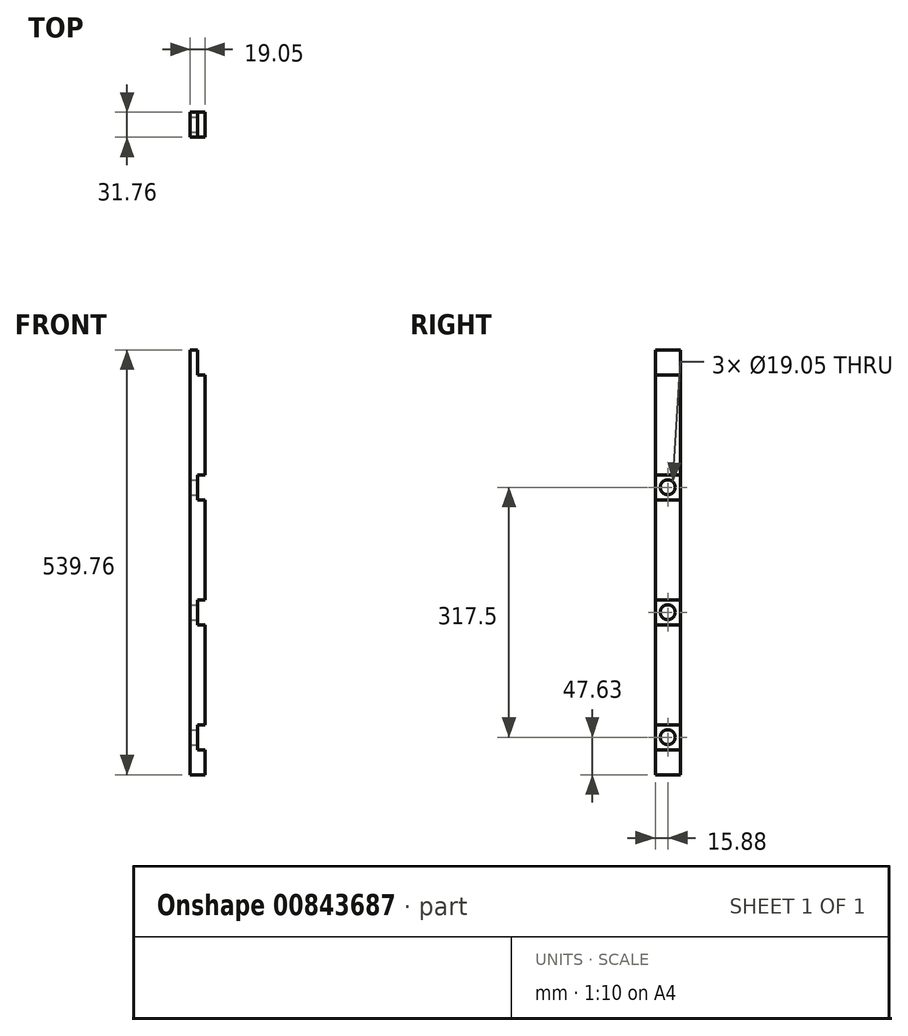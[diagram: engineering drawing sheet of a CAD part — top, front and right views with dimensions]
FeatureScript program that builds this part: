
annotation { "Feature Type Name" : "Feature", "Feature Type Description" : "" }
export const myFeature = defineFeature(function(context is Context, id is Id, definition is map)
    precondition{}
    {
        {
            var Q0;
            Q0=qCreatedBy(makeId("Right.planeOp"),FACE);
            var sketch = newSketch(context, id + "F0", { "sketchPlane" : qUnion([Q0])});
            skLineSegment(sketch, "E0.bottom", {"start": v(15.88, 269.88) * mm, "end": v(-15.87, 269.88) * mm});
            skLineSegment(sketch, "E0.top", {"start": v(15.88, -269.88) * mm, "end": v(-15.87, -269.88) * mm});
            skLineSegment(sketch, "E0.left", {"start": v(15.88, 269.88) * mm, "end": v(15.88, -269.88) * mm});
            skLineSegment(sketch, "E0.right", {"start": v(-15.87, 269.88) * mm, "end": v(-15.87, -269.88) * mm});
            skPoint(sketch, "E0.middle", {"position": v(0, 0) * mm});
            skSolve(sketch);
        }
        {
            var Q0;
            Q0 = qSketchRegion(id + "F0", true);
            extrude(context, id + "F1", {"entities" : qUnion([Q0]), "depth" : 19.05 * mm, "offsetDistance" : 25.4 * mm});
        }
        {
            var Q0;
            Q0=makeQuery(id+"F1.opExtrude","CAP_FACE",FACE,{"disambiguationData":[OSD([sQuery(id+"F0.wireOp",EDGE,"E0.bottom"),sQuery(id+"F0.wireOp",EDGE,"E0.top"),sQuery(id+"F0.wireOp",EDGE,"E0.left"),sQuery(id+"F0.wireOp",EDGE,"E0.right")])],"isStart":false});
            var sketch = newSketch(context, id + "F2", { "sketchPlane" : qUnion([Q0])});
            skLineSegment(sketch, "E1.bottom", {"start": v(-15.87, 269.88) * mm, "end": v(15.88, 269.88) * mm});
            skLineSegment(sketch, "E1.top", {"start": v(-15.87, 238.13) * mm, "end": v(15.88, 238.13) * mm});
            skLineSegment(sketch, "E1.left", {"start": v(-15.87, 269.88) * mm, "end": v(-15.87, 238.13) * mm});
            skLineSegment(sketch, "E1.right", {"start": v(15.88, 269.88) * mm, "end": v(15.88, 238.13) * mm});
            skLineSegment(sketch, "E2", {"start": v(-15.87, -269.88) * mm, "end": v(-15.87, -238.12) * mm});
            skLineSegment(sketch, "E3.bottom", {"start": v(-15.87, -238.12) * mm, "end": v(15.88, -238.12) * mm});
            skLineSegment(sketch, "E3.top", {"start": v(-15.87, -206.37) * mm, "end": v(15.88, -206.37) * mm});
            skLineSegment(sketch, "E3.left", {"start": v(-15.87, -238.12) * mm, "end": v(-15.87, -206.37) * mm});
            skLineSegment(sketch, "E3.right", {"start": v(15.88, -238.12) * mm, "end": v(15.88, -206.37) * mm});
            skLineSegment(sketch, "E4", {"start": v(-15.87, -206.37) * mm, "end": v(-15.87, -79.37) * mm});
            skLineSegment(sketch, "E5.bottom", {"start": v(-15.87, -79.37) * mm, "end": v(15.88, -79.37) * mm});
            skLineSegment(sketch, "E5.top", {"start": v(-15.87, -47.62) * mm, "end": v(15.88, -47.62) * mm});
            skLineSegment(sketch, "E5.left", {"start": v(-15.87, -79.37) * mm, "end": v(-15.87, -47.62) * mm});
            skLineSegment(sketch, "E5.right", {"start": v(15.88, -79.37) * mm, "end": v(15.88, -47.62) * mm});
            skLineSegment(sketch, "E6", {"start": v(-15.87, -47.62) * mm, "end": v(-15.87, 79.38) * mm});
            skLineSegment(sketch, "E7.bottom", {"start": v(-15.87, 79.38) * mm, "end": v(15.88, 79.38) * mm});
            skLineSegment(sketch, "E7.top", {"start": v(-15.87, 111.13) * mm, "end": v(15.88, 111.13) * mm});
            skLineSegment(sketch, "E7.left", {"start": v(-15.87, 79.38) * mm, "end": v(-15.87, 111.13) * mm});
            skLineSegment(sketch, "E7.right", {"start": v(15.88, 79.38) * mm, "end": v(15.88, 111.13) * mm});
            skSolve(sketch);
        }
        {
            var Q0;
            Q0 = qSketchRegion(id + "F2", true);
            extrude(context, id + "F3", {"entities" : qUnion([Q0]), "operationType" : NewBodyOperationType.REMOVE, "oppositeDirection" : true, "depth" : 9.52 * mm, "offsetDistance" : 25.4 * mm});
        }
        {
            var Q0;
            Q0=makeQuery(id+"F3.boolean.opBoolean","COPY",FACE,{"derivedFrom":makeQuery(id+"F3.opExtrude","CAP_FACE",FACE,{"disambiguationData":[OSD([sQuery(id+"F2.wireOp",EDGE,"E7.bottom"),sQuery(id+"F2.wireOp",EDGE,"E7.top"),sQuery(id+"F2.wireOp",EDGE,"E7.left"),sQuery(id+"F2.wireOp",EDGE,"E7.right")])],"isStart":false})});
            var sketch = newSketch(context, id + "F4", { "sketchPlane" : qUnion([Q0])});
            skLineSegment(sketch, "E8", {"start": v(-15.87, 79.38) * mm, "end": v(15.88, 111.13) * mm});
            skCircle(sketch, "E9", {"center": v(0, 95.25) * mm, "radius": 9.53 * mm});
            skSolve(sketch);
        }
        {
            var Q0;
            Q0 = qSketchRegion(id + "F4", true);
            extrude(context, id + "F5", {"entities" : qUnion([Q0]), "operationType" : NewBodyOperationType.REMOVE, "oppositeDirection" : true, "depth" : 25.4 * mm, "offsetDistance" : 25.4 * mm});
        }
        {
            var Q0;
            Q0=makeQuery(id+"F3.boolean.opBoolean","COPY",FACE,{"derivedFrom":makeQuery(id+"F3.opExtrude","CAP_FACE",FACE,{"disambiguationData":[OSD([sQuery(id+"F2.wireOp",EDGE,"E5.bottom"),sQuery(id+"F2.wireOp",EDGE,"E5.top"),sQuery(id+"F2.wireOp",EDGE,"E5.left"),sQuery(id+"F2.wireOp",EDGE,"E5.right")])],"isStart":false})});
            var sketch = newSketch(context, id + "F6", { "sketchPlane" : qUnion([Q0])});
            skLineSegment(sketch, "E10", {"start": v(-15.87, -79.37) * mm, "end": v(15.88, -47.62) * mm});
            skCircle(sketch, "E11", {"center": v(0, -63.5) * mm, "radius": 9.53 * mm});
            skSolve(sketch);
        }
        {
            var Q0;
            Q0 = qSketchRegion(id + "F6", true);
            extrude(context, id + "F7", {"entities" : qUnion([Q0]), "operationType" : NewBodyOperationType.REMOVE, "oppositeDirection" : true, "depth" : 25.4 * mm, "offsetDistance" : 25.4 * mm});
        }
        {
            var Q0;
            Q0=makeQuery(id+"F3.boolean.opBoolean","COPY",FACE,{"derivedFrom":makeQuery(id+"F3.opExtrude","CAP_FACE",FACE,{"disambiguationData":[OSD([sQuery(id+"F2.wireOp",EDGE,"E3.bottom"),sQuery(id+"F2.wireOp",EDGE,"E3.top"),sQuery(id+"F2.wireOp",EDGE,"E3.left"),sQuery(id+"F2.wireOp",EDGE,"E3.right")])],"isStart":false})});
            var sketch = newSketch(context, id + "F8", { "sketchPlane" : qUnion([Q0])});
            skLineSegment(sketch, "E12", {"start": v(-15.87, -238.12) * mm, "end": v(15.88, -206.37) * mm});
            skCircle(sketch, "E13", {"center": v(0, -222.25) * mm, "radius": 9.53 * mm});
            skSolve(sketch);
        }
        {
            var Q0;
            Q0 = qSketchRegion(id + "F8", true);
            extrude(context, id + "F9", {"entities" : qUnion([Q0]), "operationType" : NewBodyOperationType.REMOVE, "oppositeDirection" : true, "depth" : 25.4 * mm, "offsetDistance" : 25.4 * mm});
        }
    });
